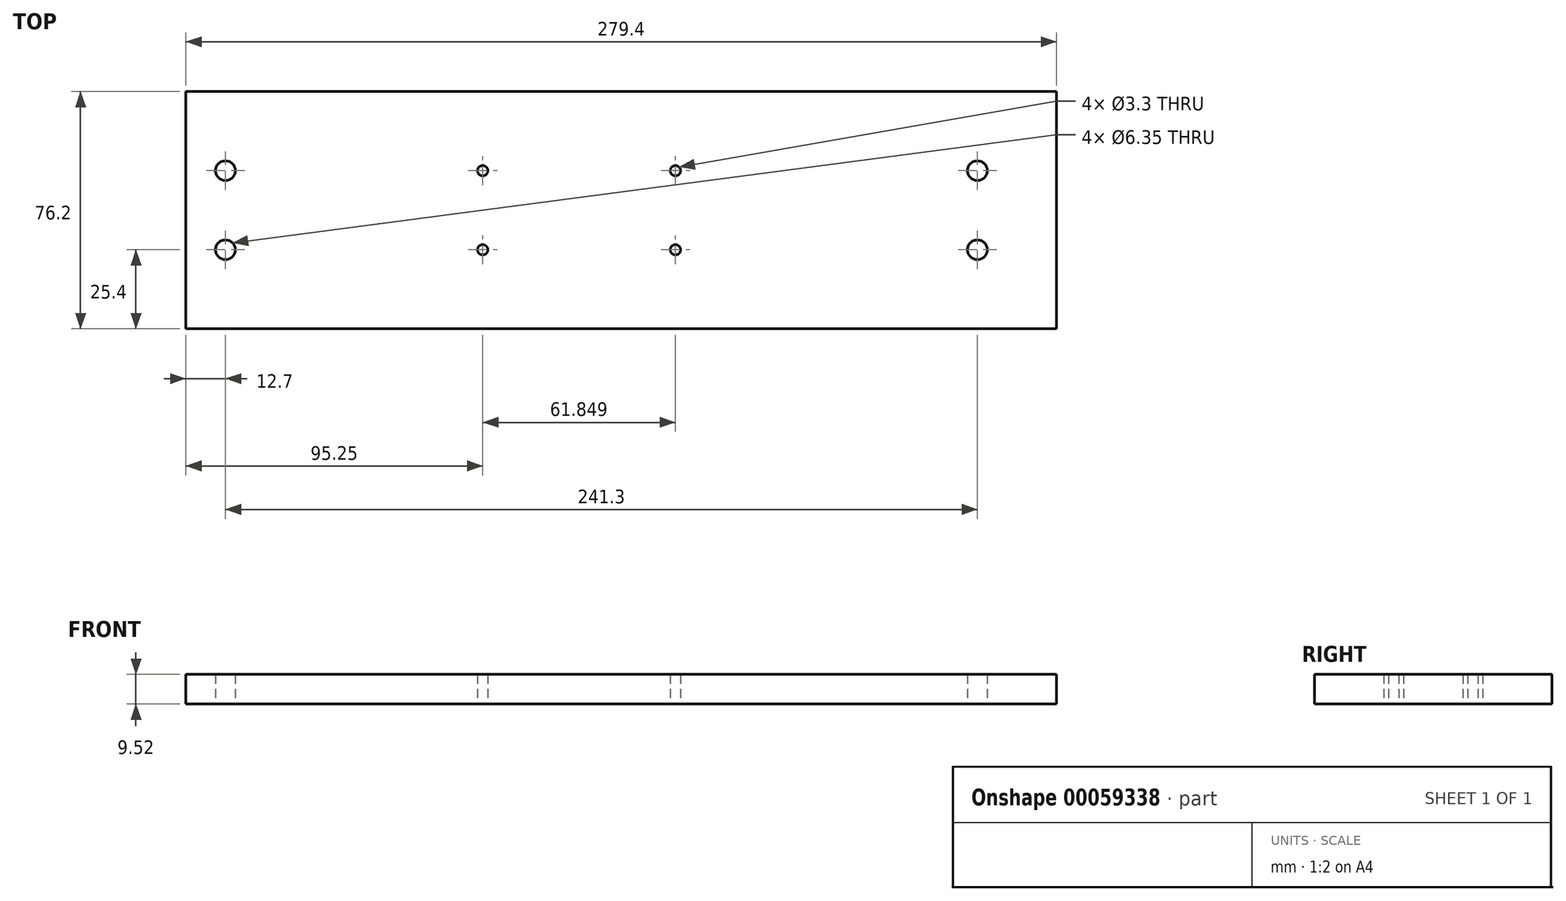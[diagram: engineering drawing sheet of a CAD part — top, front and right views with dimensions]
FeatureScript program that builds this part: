
annotation { "Feature Type Name" : "Feature", "Feature Type Description" : "" }
export const myFeature = defineFeature(function(context is Context, id is Id, definition is map)
    precondition{}
    {
        {
            var Q0;
            Q0=qCreatedBy(makeId("Top.planeOp"),FACE);
            var sketch = newSketch(context, id + "F0", { "sketchPlane" : qUnion([Q0])});
            skLineSegment(sketch, "E0.bottom", {"start": v(-152.4, -38.1) * mm, "end": v(127, -38.1) * mm});
            skLineSegment(sketch, "E0.top", {"start": v(-152.4, 38.1) * mm, "end": v(127, 38.1) * mm});
            skLineSegment(sketch, "E0.left", {"start": v(-152.4, -38.1) * mm, "end": v(-152.4, 38.1) * mm});
            skLineSegment(sketch, "E0.right", {"start": v(127, -38.1) * mm, "end": v(127, 38.1) * mm});
            skCircle(sketch, "E1", {"center": v(101.6, 12.7) * mm, "radius": 3.18 * mm});
            skCircle(sketch, "E2", {"center": v(4.7, 12.7) * mm, "radius": 1.65 * mm});
            skCircle(sketch, "E3", {"center": v(-57.15, 12.7) * mm, "radius": 1.65 * mm});
            skCircle(sketch, "E4", {"center": v(-139.7, 12.7) * mm, "radius": 3.18 * mm});
            skCircle(sketch, "E5.MirrorC", {"center": v(-139.7, -12.7) * mm, "radius": 3.18 * mm});
            skCircle(sketch, "E6.MirrorC", {"center": v(4.7, -12.7) * mm, "radius": 1.65 * mm});
            skCircle(sketch, "E7.MirrorC", {"center": v(-57.15, -12.7) * mm, "radius": 1.65 * mm});
            skCircle(sketch, "E8.MirrorC", {"center": v(101.6, -12.7) * mm, "radius": 3.18 * mm});
            skSolve(sketch);
        }
        {
            var Q0;
            Q0 = qSketchRegion(id + "F0", true);
            extrude(context, id + "F1", {"entities" : qUnion([Q0]), "endBound" : BoundingType.SYMMETRIC, "depth" : 9.52 * mm});
        }
    });
